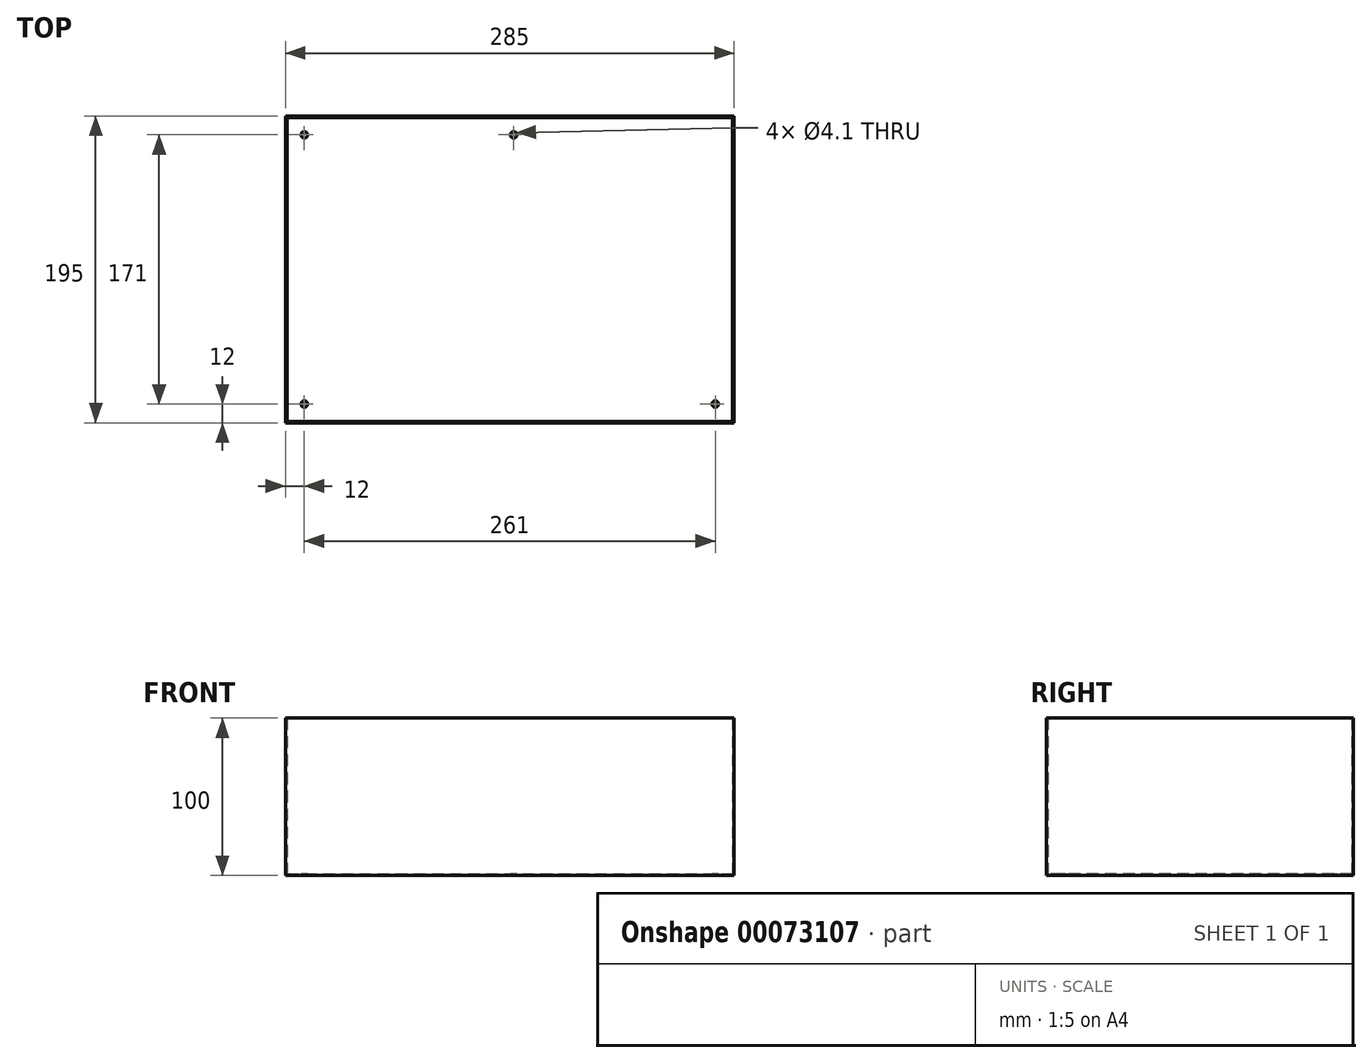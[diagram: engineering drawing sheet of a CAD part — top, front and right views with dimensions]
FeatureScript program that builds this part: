
annotation { "Feature Type Name" : "Feature", "Feature Type Description" : "" }
export const myFeature = defineFeature(function(context is Context, id is Id, definition is map)
    precondition{}
    {
        {
            var Q0;
            Q0=qCreatedBy(makeId("Top.planeOp"),FACE);
            var sketch = newSketch(context, id + "F0", { "sketchPlane" : qUnion([Q0])});
            skLineSegment(sketch, "E0.rect.bottom", {"start": v(-130, 100) * mm, "end": v(155, 100) * mm});
            skLineSegment(sketch, "E0.rect.top", {"start": v(-130, -95) * mm, "end": v(155, -95) * mm});
            skLineSegment(sketch, "E0.rect.left", {"start": v(-130, 100) * mm, "end": v(-130, -95) * mm});
            skLineSegment(sketch, "E0.rect.right", {"start": v(155, 100) * mm, "end": v(155, -95) * mm});
            skPoint(sketch, "E1", {"position": v(143, -83) * mm});
            skPoint(sketch, "E2", {"position": v(-118, -83) * mm});
            skPoint(sketch, "E3", {"position": v(-118, 88) * mm});
            skPoint(sketch, "E4", {"position": v(15, 88) * mm});
            skSolve(sketch);
        }
        {
            var Q0;
            Q0=makeQuery(id+"F0.imprint","IMPRINT",FACE,{"disambiguationData":[TD([[makeQuery(id+"F0.imprint","IMPRINT",EDGE,{"derivedFrom":sQuery(id+"F0.wireOp",EDGE,"E0.rect.bottom")}),-1.0]])]});
            var Q1;
            Q1=makeQuery(id+"F0.imprint","IMPRINT",FACE,{"disambiguationData":[TD([[makeQuery(id+"F0.imprint","IMPRINT",EDGE,{"derivedFrom":sQuery(id+"F0.wireOp",EDGE,"93b45e06-8040-4340-91bb-dc44525623ce")}),-1.0]])]});
            var Q2;
            Q2=makeQuery(id+"F0.imprint","IMPRINT",FACE,{"disambiguationData":[TD([[makeQuery(id+"F0.imprint","IMPRINT",EDGE,{"derivedFrom":sQuery(id+"F0.wireOp",EDGE,"b6a39dd8-fad0-4eb4-adf2-3012210b0292.bottom")}),1.0]])]});
            var Q3;
            Q3=makeQuery(id+"F0.imprint","IMPRINT",FACE,{"disambiguationData":[TD([[makeQuery(id+"F0.imprint","IMPRINT",EDGE,{"derivedFrom":sQuery(id+"F0.wireOp",EDGE,"4c31caf5-2bcb-42db-99db-2e25951ee86a")}),1.0]])]});
            var Q4;
            Q4=makeQuery(id+"F0.imprint","IMPRINT",FACE,{"disambiguationData":[TD([[makeQuery(id+"F0.imprint","IMPRINT",EDGE,{"derivedFrom":sQuery(id+"F0.wireOp",EDGE,"93b45e06-8040-4340-91bb-dc44525623ce")}),1.0]])]});
            var Q5;
            Q5=makeQuery(id+"F0.imprint","IMPRINT",FACE,{"disambiguationData":[TD([[makeQuery(id+"F0.imprint","IMPRINT",EDGE,{"derivedFrom":sQuery(id+"F0.wireOp",EDGE,"04952d9e-528b-47e6-835d-ede1efc0ccc2")}),1.0]])]});
            var Q6;
            Q6=makeQuery(id+"F0.imprint","IMPRINT",FACE,{"disambiguationData":[TD([[makeQuery(id+"F0.imprint","IMPRINT",EDGE,{"derivedFrom":sQuery(id+"F0.wireOp",EDGE,"4f8f6633-d96a-440b-b4b0-11e18a34e8bf")}),1.0]])]});
            var Q7;
            Q7=makeQuery(id+"F0.imprint","IMPRINT",FACE,{"disambiguationData":[TD([[makeQuery(id+"F0.imprint","IMPRINT",EDGE,{"derivedFrom":sQuery(id+"F0.wireOp",EDGE,"6689d007-ad82-4502-a3dc-1998c5ef634e")}),1.0]])]});
            extrude(context, id + "F1", {"entities" : qUnion([Q0, Q1, Q2, Q3, Q4, Q5, Q6, Q7]), "depth" : 100 * mm});
        }
        {
            var Q0;
            Q0=makeQuery(id+"F1.opExtrude","CAP_FACE",FACE,{"disambiguationData":[OSD([sQuery(id+"F0.wireOp",EDGE,"E0.rect.bottom"),sQuery(id+"F0.wireOp",EDGE,"E0.rect.top"),sQuery(id+"F0.wireOp",EDGE,"E0.rect.left"),sQuery(id+"F0.wireOp",EDGE,"E0.rect.right")])],"isStart":false});
            shell(context, id + "F2", {"entities" : qUnion([Q0]), "thickness" : 1 * mm});
        }
        {
            var Q0;
            Q0=sQuery(id+"F0.wireOp",VERTEX,"E4");
            var Q1;
            Q1=sQuery(id+"F0.wireOp",VERTEX,"E3");
            var Q2;
            Q2=sQuery(id+"F0.wireOp",VERTEX,"E1");
            var Q3;
            Q3=sQuery(id+"F0.wireOp",VERTEX,"E2");
            var Q4;
            Q4=makeQuery(id+"F1.opExtrude","SWEPT_BODY",BODY,{"disambiguationData":[OSD([sQuery(id+"F0.wireOp",EDGE,"E0.rect.bottom"),sQuery(id+"F0.wireOp",EDGE,"E0.rect.top"),sQuery(id+"F0.wireOp",EDGE,"E0.rect.left"),sQuery(id+"F0.wireOp",EDGE,"E0.rect.right")])]});
            hole(context, id + "F3", {"style" : HoleStyle.SIMPLE, "endStyle" : HoleEndStyle.THROUGH, "oppositeDirection" : true, "standardTappedOrClearance" : lookupTablePath({ "standard" : "ISO", "size" : "4.1", "type" : "Drilled" }), "standardBlindInLast" : lookupTablePath({ "standard" : "ISO", "size" : "4.1", "type" : "Drilled" }), "holeDiameter" : 4.1 * mm, "locations" : qUnion([Q0, Q1, Q2, Q3]), "scope" : qUnion([Q4]), "isTappedThrough" : true});
        }
    });
